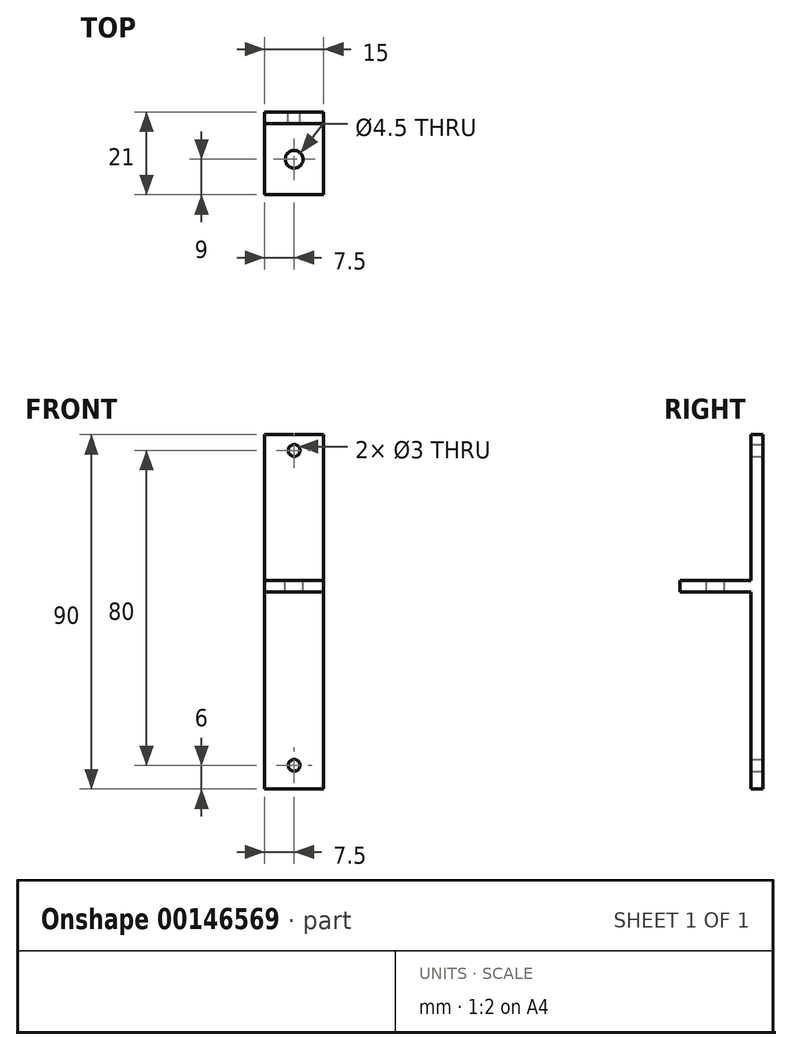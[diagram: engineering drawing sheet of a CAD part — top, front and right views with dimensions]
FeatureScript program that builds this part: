
annotation { "Feature Type Name" : "Feature", "Feature Type Description" : "" }
export const myFeature = defineFeature(function(context is Context, id is Id, definition is map)
    precondition{}
    {
        {
            var Q0;
            Q0=qCreatedBy(makeId("Front.planeOp"),FACE);
            var sketch = newSketch(context, id + "F0", { "sketchPlane" : qUnion([Q0])});
            skLineSegment(sketch, "E0.bottom", {"start": v(7.5, -45) * mm, "end": v(-7.5, -45) * mm});
            skLineSegment(sketch, "E0.top", {"start": v(7.5, 45) * mm, "end": v(-7.5, 45) * mm});
            skLineSegment(sketch, "E0.left", {"start": v(7.5, -45) * mm, "end": v(7.5, 45) * mm});
            skLineSegment(sketch, "E0.right", {"start": v(-7.5, -45) * mm, "end": v(-7.5, 45) * mm});
            skPoint(sketch, "E0.middle", {"position": v(0, 0) * mm});
            skLineSegment(sketch, "E1", {"start": v(0, 45) * mm, "end": v(0, -45) * mm, "construction": true});
            skLineSegment(sketch, "E2", {"start": v(-7.5, 5) * mm, "end": v(7.5, 5) * mm, "construction": true});
            skCircle(sketch, "E3", {"center": v(0, 41) * mm, "radius": 1.5 * mm});
            skCircle(sketch, "E4", {"center": v(0, -39) * mm, "radius": 1.5 * mm});
            skSolve(sketch);
        }
        {
            var Q0;
            Q0=qSketchRegion(id+"F0",true);
            extrude(context, id + "F1", {"entities" : qUnion([Q0]), "depth" : 3 * mm});
        }
        {
            var Q0;
            Q0=makeQuery(id+"F1.opExtrude","CAP_FACE",FACE,{"disambiguationData":[OSD([sQuery(id+"F0.wireOp",EDGE,"E0.bottom"),sQuery(id+"F0.wireOp",EDGE,"E0.top"),sQuery(id+"F0.wireOp",EDGE,"E0.left"),sQuery(id+"F0.wireOp",EDGE,"E0.right"),sQuery(id+"F0.wireOp",EDGE,"E3"),sQuery(id+"F0.wireOp",EDGE,"E4")])],"isStart":false});
            var sketch = newSketch(context, id + "F2", { "sketchPlane" : qUnion([Q0])});
            skLineSegment(sketch, "E5.bottom", {"start": v(7.5, 8) * mm, "end": v(-7.5, 8) * mm});
            skLineSegment(sketch, "E5.top", {"start": v(7.5, 5) * mm, "end": v(-7.5, 5) * mm});
            skLineSegment(sketch, "E5.left", {"start": v(7.5, 8) * mm, "end": v(7.5, 5) * mm});
            skLineSegment(sketch, "E5.right", {"start": v(-7.5, 8) * mm, "end": v(-7.5, 5) * mm});
            skPoint(sketch, "E5.middle", {"position": v(0, 6.5) * mm});
            skSolve(sketch);
        }
        {
            var Q0;
            Q0=qSketchRegion(id+"F2",true);
            extrude(context, id + "F3", {"entities" : qUnion([Q0]), "operationType" : NewBodyOperationType.ADD, "depth" : 18 * mm});
        }
        {
            var Q0;
            Q0=makeQuery(id+"F3.opExtrude","SWEPT_FACE",FACE,{"disambiguationData":[OSD([sQuery(id+"F2.wireOp",EDGE,"E5.bottom")])]});
            var sketch = newSketch(context, id + "F4", { "sketchPlane" : qUnion([Q0])});
            skLineSegment(sketch, "E6", {"start": v(-7.5, -12) * mm, "end": v(7.5, -12) * mm, "construction": true});
            skLineSegment(sketch, "E7", {"start": v(0, -21) * mm, "end": v(0, 0) * mm, "construction": true});
            skCircle(sketch, "E8", {"center": v(0, -12) * mm, "radius": 2.25 * mm});
            skSolve(sketch);
        }
        {
            var Q0;
            Q0=qSketchRegion(id+"F4",true);
            extrude(context, id + "F5", {"entities" : qUnion([Q0]), "operationType" : NewBodyOperationType.REMOVE, "endBound" : BoundingType.THROUGH_ALL, "oppositeDirection" : true, "depth" : 25 * mm});
        }
    });
